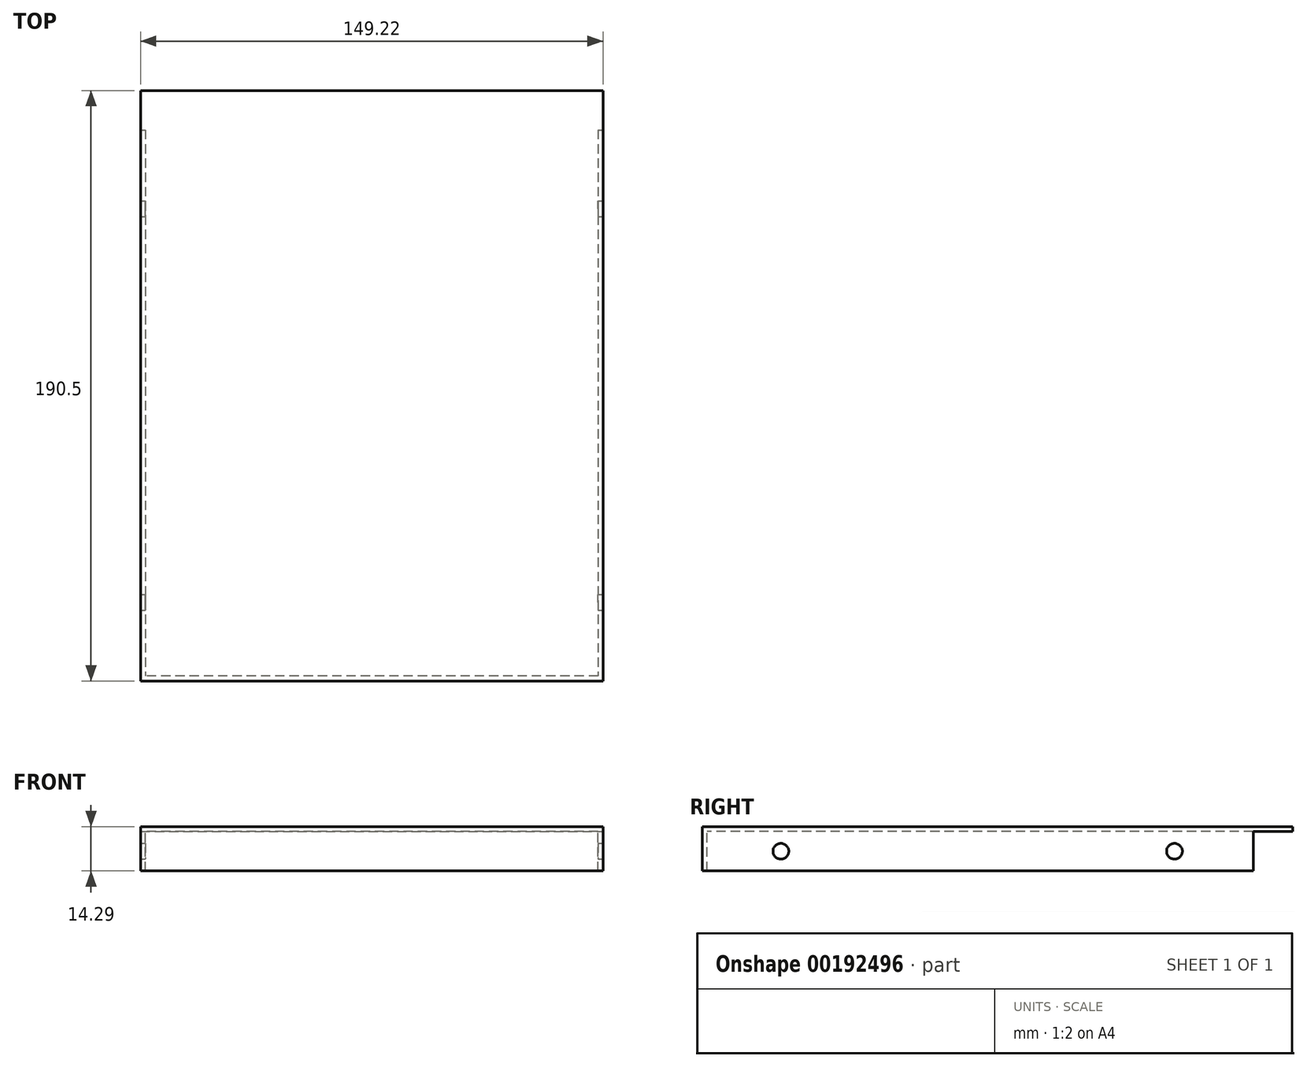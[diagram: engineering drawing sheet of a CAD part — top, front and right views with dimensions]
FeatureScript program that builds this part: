
annotation { "Feature Type Name" : "Feature", "Feature Type Description" : "" }
export const myFeature = defineFeature(function(context is Context, id is Id, definition is map)
    precondition{}
    {
        {
            var Q0;
            Q0=qCreatedBy(makeId("Top.planeOp"),FACE);
            cPlane(context, id + "F0", {"entities" : qUnion([Q0]), "cplaneType" : CPlaneType.OFFSET, "offset" : 92.07 * mm, "width" : 152.4 * mm, "height" : 152.4 * mm});
        }
        {
            var Q0;
            Q0=qCreatedBy(id+"F0.planeOp",FACE);
            cPlane(context, id + "F1", {"entities" : qUnion([Q0]), "cplaneType" : CPlaneType.OFFSET, "offset" : 95.25 * mm, "width" : 152.4 * mm, "height" : 152.4 * mm});
        }
        {
            var Q0;
            Q0=qCreatedBy(id+"F1.planeOp",FACE);
            var sketch = newSketch(context, id + "F2", { "sketchPlane" : qUnion([Q0])});
            skLineSegment(sketch, "E0.0", {"start": v(-73.03, 223.84) * mm, "end": v(-73.03, 47.63) * mm});
            skLineSegment(sketch, "E0.1", {"start": v(73.02, 47.63) * mm, "end": v(-73.03, 47.63) * mm});
            skLineSegment(sketch, "E0.2", {"start": v(73.02, 223.84) * mm, "end": v(73.02, 47.63) * mm});
            skLineSegment(sketch, "E1.0", {"start": v(74.61, 223.84) * mm, "end": v(74.61, 46.04) * mm});
            skLineSegment(sketch, "E1.1", {"start": v(74.61, 46.04) * mm, "end": v(-74.61, 46.04) * mm});
            skLineSegment(sketch, "E1.2", {"start": v(-74.61, 223.84) * mm, "end": v(-74.61, 46.04) * mm});
            skLineSegment(sketch, "E2", {"start": v(-74.61, 223.84) * mm, "end": v(-73.03, 223.84) * mm});
            skLineSegment(sketch, "E3", {"start": v(73.02, 223.84) * mm, "end": v(74.61, 223.84) * mm});
            skSolve(sketch);
        }
        {
            var Q0;
            Q0 = qSketchRegion(id + "F2", true);
            extrude(context, id + "F3", {"entities" : qUnion([Q0]), "oppositeDirection" : true, "depth" : 12.7 * mm});
        }
        {
            var Q0;
            Q0=makeQuery(id+"F3.opExtrude","CAP_FACE",FACE,{"disambiguationData":[OSD([sQuery(id+"F2.wireOp",EDGE,"E0.0"),sQuery(id+"F2.wireOp",EDGE,"E0.1"),sQuery(id+"F2.wireOp",EDGE,"E0.2"),sQuery(id+"F2.wireOp",EDGE,"E1.0"),sQuery(id+"F2.wireOp",EDGE,"E1.1"),sQuery(id+"F2.wireOp",EDGE,"E1.2"),sQuery(id+"F2.wireOp",EDGE,"E2"),sQuery(id+"F2.wireOp",EDGE,"E3")])],"isStart":true});
            var sketch = newSketch(context, id + "F4", { "sketchPlane" : qUnion([Q0])});
            skLineSegment(sketch, "E4.top", {"start": v(74.61, 46.04) * mm, "end": v(-74.61, 46.04) * mm});
            skLineSegment(sketch, "E4.left", {"start": v(74.61, 223.84) * mm, "end": v(74.61, 46.04) * mm});
            skLineSegment(sketch, "E4.right", {"start": v(-74.61, 223.84) * mm, "end": v(-74.61, 46.04) * mm});
            skLineSegment(sketch, "E5", {"start": v(-74.61, 223.84) * mm, "end": v(-74.61, 236.54) * mm});
            skLineSegment(sketch, "E6", {"start": v(-74.61, 236.54) * mm, "end": v(74.61, 236.54) * mm});
            skLineSegment(sketch, "E7", {"start": v(74.61, 236.54) * mm, "end": v(74.61, 223.84) * mm});
            skSolve(sketch);
        }
        {
            var Q0;
            Q0 = qSketchRegion(id + "F4", true);
            extrude(context, id + "F5", {"entities" : qUnion([Q0]), "operationType" : NewBodyOperationType.ADD, "depth" : 1.59 * mm});
        }
        {
            var Q0;
            Q0=makeQuery(id+"F5.boolean.opBoolean","MERGE",FACE,{"derivedFrom":[makeQuery(id+"F3.opExtrude","SWEPT_FACE",FACE,{"disambiguationData":[OSD([sQuery(id+"F2.wireOp",EDGE,"E1.0")])]}),makeQuery(id+"F5.opExtrude","SWEPT_FACE",FACE,{"disambiguationData":[OSD([sQuery(id+"F4.wireOp",EDGE,"E4.left"),sQuery(id+"F4.wireOp",EDGE,"E7")])]})]});
            var sketch = newSketch(context, id + "F6", { "sketchPlane" : qUnion([Q0])});
            skCircle(sketch, "E8", {"center": v(71.44, 180.98) * mm, "radius": 2.55 * mm});
            skCircle(sketch, "E9.1.0.0", {"center": v(198.44, 180.98) * mm, "radius": 2.55 * mm});
            skLineSegment(sketch, "E9.direction1", {"start": v(71.44, 180.98) * mm, "end": v(198.44, 180.98) * mm, "construction": true});
            skSolve(sketch);
        }
        {
            var Q0;
            Q0 = qSketchRegion(id + "F6", true);
            extrude(context, id + "F7", {"entities" : qUnion([Q0]), "operationType" : NewBodyOperationType.REMOVE, "endBound" : BoundingType.THROUGH_ALL, "oppositeDirection" : true, "depth" : 25.4 * mm});
        }
    });
